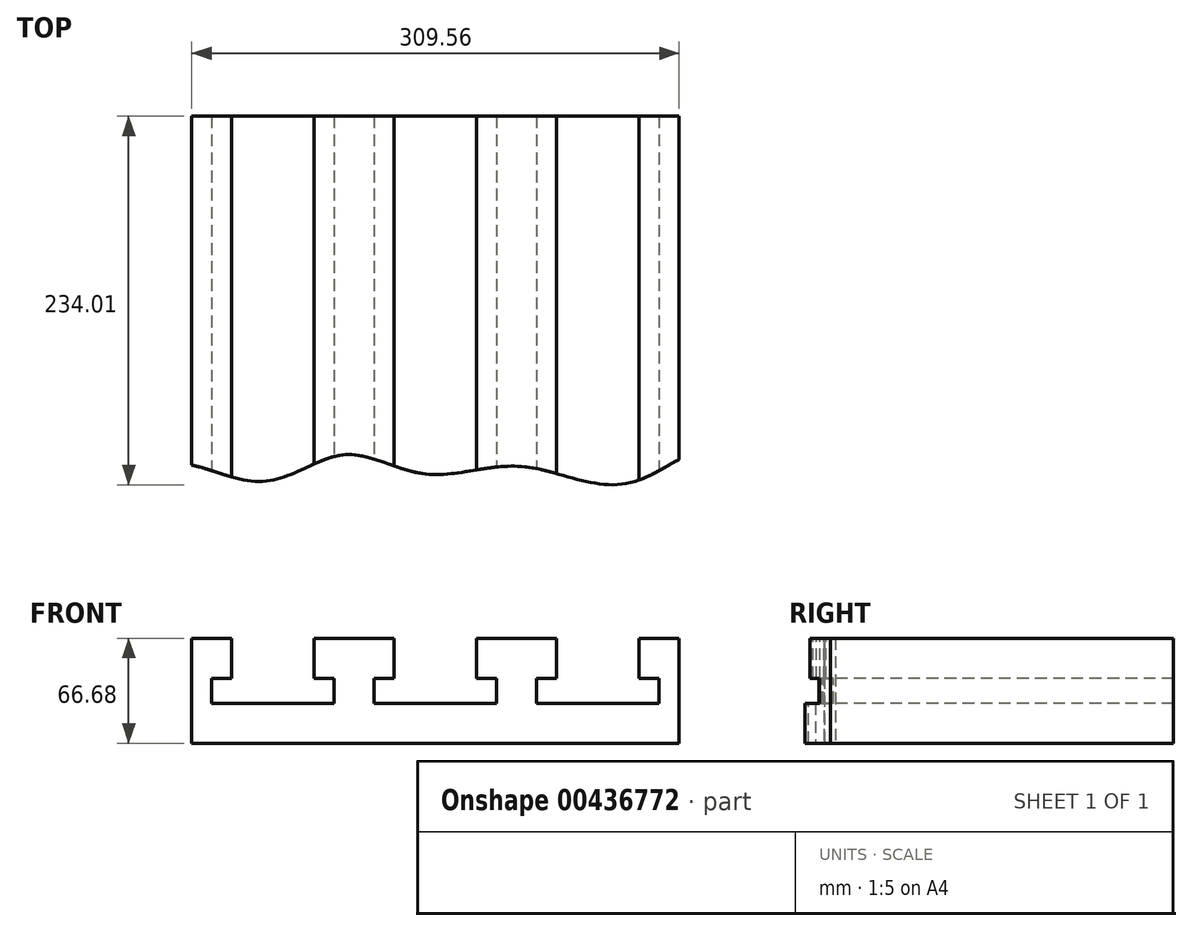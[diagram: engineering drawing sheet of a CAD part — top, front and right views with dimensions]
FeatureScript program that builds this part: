
annotation { "Feature Type Name" : "Feature", "Feature Type Description" : "" }
export const myFeature = defineFeature(function(context is Context, id is Id, definition is map)
    precondition{}
    {
        {
            var Q0;
            Q0=qCreatedBy(makeId("Front.planeOp"),FACE);
            var sketch = newSketch(context, id + "F0", { "sketchPlane" : qUnion([Q0])});
            skLineSegment(sketch, "E0.MirrorCS", {"start": v(-77, 53.7) * mm, "end": v(-77, 28.3) * mm});
            skLineSegment(sketch, "E1.MirrorCS", {"start": v(-64.3, 12.43) * mm, "end": v(-142.08, 12.43) * mm});
            skLineSegment(sketch, "E2.MirrorCS", {"start": v(-142.08, 28.3) * mm, "end": v(-142.08, 12.43) * mm});
            skLineSegment(sketch, "E3.MirrorCS", {"start": v(-154.78, 53.7) * mm, "end": v(-154.78, -12.97) * mm});
            skLineSegment(sketch, "E4.MirrorCS", {"start": v(-129.38, 28.3) * mm, "end": v(-142.08, 28.3) * mm});
            skLineSegment(sketch, "E5.MirrorCS", {"start": v(-129.38, 53.7) * mm, "end": v(-129.38, 28.3) * mm});
            skLineSegment(sketch, "E6.MirrorCS", {"start": v(-64.3, 28.3) * mm, "end": v(-77, 28.3) * mm});
            skLineSegment(sketch, "E7.MirrorCS", {"start": v(-64.3, 28.3) * mm, "end": v(-64.3, 12.43) * mm});
            skLineSegment(sketch, "E8.MirrorCS", {"start": v(-38.9, 28.3) * mm, "end": v(-38.9, 12.43) * mm});
            skLineSegment(sketch, "E9.MirrorCS", {"start": v(26.2, 53.7) * mm, "end": v(26.2, 28.3) * mm});
            skLineSegment(sketch, "E10.MirrorCS", {"start": v(-38.9, 12.43) * mm, "end": v(38.9, 12.43) * mm});
            skLineSegment(sketch, "E11.MirrorCS", {"start": v(-26.2, 53.7) * mm, "end": v(-26.2, 28.3) * mm});
            skLineSegment(sketch, "E12.MirrorCS", {"start": v(38.9, 28.3) * mm, "end": v(38.9, 12.43) * mm});
            skLineSegment(sketch, "E13.MirrorCS", {"start": v(-38.9, 28.3) * mm, "end": v(-26.2, 28.3) * mm});
            skLineSegment(sketch, "E14.MirrorCS", {"start": v(26.2, 28.3) * mm, "end": v(38.9, 28.3) * mm});
            skLineSegment(sketch, "E15.MirrorCS", {"start": v(77, 53.7) * mm, "end": v(77, 28.3) * mm});
            skLineSegment(sketch, "E16.MirrorCS", {"start": v(77, 28.3) * mm, "end": v(64.3, 28.3) * mm});
            skLineSegment(sketch, "E17.MirrorCS", {"start": v(142.08, 12.43) * mm, "end": v(64.3, 12.43) * mm});
            skLineSegment(sketch, "E18.MirrorCS", {"start": v(64.3, 28.3) * mm, "end": v(64.3, 12.43) * mm});
            skLineSegment(sketch, "E19.MirrorCS", {"start": v(129.38, 53.7) * mm, "end": v(129.38, 28.3) * mm});
            skLineSegment(sketch, "E20.MirrorCS", {"start": v(142.08, 28.3) * mm, "end": v(129.38, 28.3) * mm});
            skLineSegment(sketch, "E21.MirrorCS", {"start": v(142.08, 28.3) * mm, "end": v(142.08, 12.43) * mm});
            skLineSegment(sketch, "E22", {"start": v(154.78, 53.7) * mm, "end": v(154.78, -12.97) * mm});
            skLineSegment(sketch, "E23.trimOffspring", {"start": v(-77, 53.7) * mm, "end": v(-26.2, 53.7) * mm});
            skLineSegment(sketch, "E24.trimOffspring", {"start": v(129.38, 53.7) * mm, "end": v(154.78, 53.7) * mm});
            skLineSegment(sketch, "E25.trimOffspring", {"start": v(26.2, 53.7) * mm, "end": v(77, 53.7) * mm});
            skLineSegment(sketch, "E26", {"start": v(-154.78, 53.7) * mm, "end": v(-129.38, 53.7) * mm});
            skLineSegment(sketch, "E27", {"start": v(-154.78, -12.97) * mm, "end": v(154.78, -12.97) * mm});
            skSolve(sketch);
        }
        {
            var Q0;
            Q0=makeQuery(id+"F0.imprint","IMPRINT",FACE,{"disambiguationData":[TD([[makeQuery(id+"F0.imprint","IMPRINT",EDGE,{"derivedFrom":sQuery(id+"F0.wireOp",EDGE,"E0.MirrorCS")}),1.0]])]});
            extrude(context, id + "F1", {"entities" : qUnion([Q0]), "oppositeDirection" : true, "depth" : 254 * mm});
        }
        {
            var Q0;
            Q0=makeQuery(id+"F1.opExtrude","SWEPT_FACE",FACE,{"disambiguationData":[OSD([sQuery(id+"F0.wireOp",EDGE,"E26")])]});
            var sketch = newSketch(context, id + "F2", { "sketchPlane" : qUnion([Q0])});
            skFitSpline(sketch, "E28", {"points": [v(-172.58, 31.05) * mm, v(-176.83, -52.48) * mm, v(43.41, -89.72) * mm, v(197.7, -13.11) * mm, v(196.2, 17.38) * mm, v(174.9, 42.94) * mm, v(122.15, 20.94) * mm, v(54.58, 31.58) * mm, v(-6.6, 26.79) * mm, v(-58.2, 39.03) * mm, v(-112.46, 22) * mm, v(-172.58, 31.05) * mm]});
            skSolve(sketch);
        }
        {
            var Q0;
            {var subQ1=sQuery(id+"F0.wireOp",EDGE,"E26");var subQ6=makeQuery(id+"F1.opExtrude","CAP_EDGE",EDGE,{"disambiguationData":[OSD([subQ1])],"isStart":true});Q0=makeQuery(id+"F2.imprint","IMPRINT",FACE,{"disambiguationData":[TD([[makeQuery(id+"F2.imprint","IMPRINT",EDGE,{"derivedFrom":subQ6}),-1.0]])]});}
            var Q1;
            {var subQ1=sQuery(id+"F0.wireOp",EDGE,"E26");var subQ6=makeQuery(id+"F1.opExtrude","CAP_EDGE",EDGE,{"disambiguationData":[OSD([subQ1])],"isStart":true});Q1=makeQuery(id+"F2.imprint","IMPRINT",FACE,{"disambiguationData":[TD([[makeQuery(id+"F2.imprint","IMPRINT",EDGE,{"derivedFrom":subQ6}),1.0]])]});}
            extrude(context, id + "F3", {"entities" : qUnion([Q0, Q1]), "operationType" : NewBodyOperationType.REMOVE, "endBound" : BoundingType.THROUGH_ALL, "oppositeDirection" : true, "depth" : 25.4 * mm});
        }
    });
